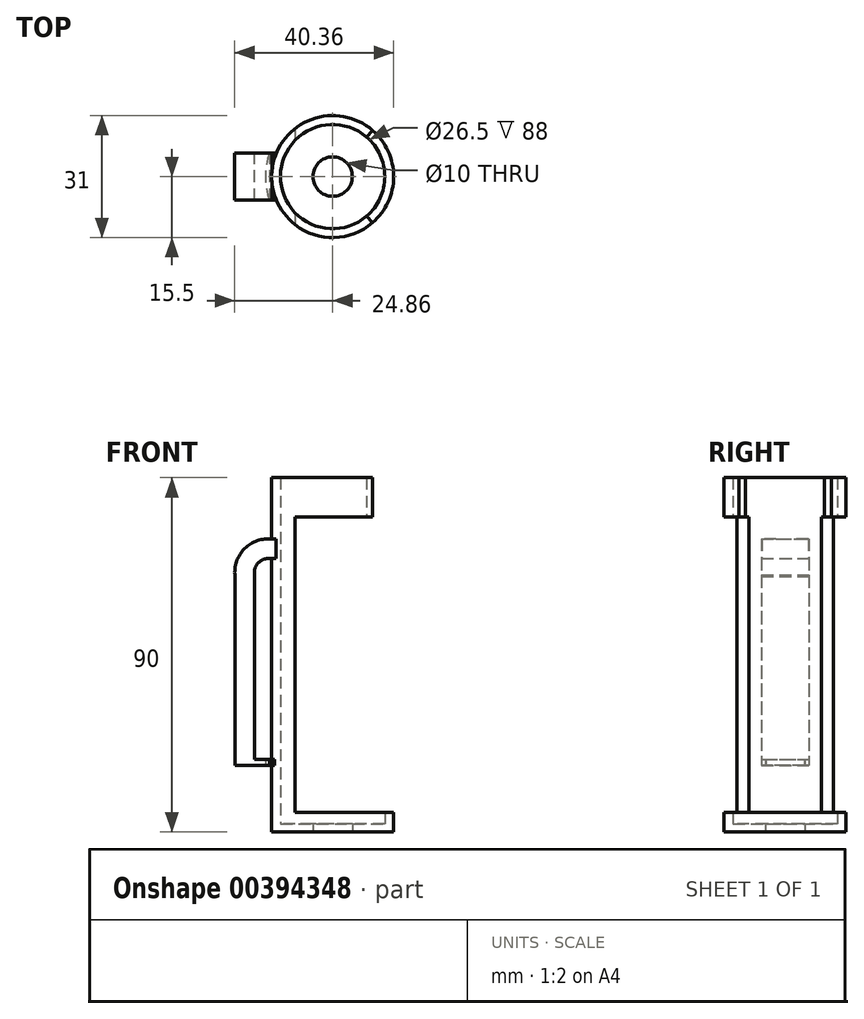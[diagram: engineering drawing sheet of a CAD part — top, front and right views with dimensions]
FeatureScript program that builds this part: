
annotation { "Feature Type Name" : "Feature", "Feature Type Description" : "" }
export const myFeature = defineFeature(function(context is Context, id is Id, definition is map)
    precondition{}
    {
        {
            var Q0;
            Q0=qCreatedBy(makeId("Top.planeOp"),FACE);
            var sketch = newSketch(context, id + "F0", { "sketchPlane" : qUnion([Q0])});
            skCircle(sketch, "E0", {"center": v(0, 0) * mm, "radius": 13.25 * mm});
            skCircle(sketch, "E1", {"center": v(0, 0) * mm, "radius": 15.5 * mm});
            skSolve(sketch);
        }
        {
            var Q0;
            Q0 = qSketchRegion(id + "F0", true);
            extrude(context, id + "F1", {"entities" : qUnion([Q0]), "depth" : 90 * mm});
        }
        {
            var Q0;
            Q0=qCreatedBy(makeId("Top.planeOp"),FACE);
            var sketch = newSketch(context, id + "F2", { "sketchPlane" : qUnion([Q0])});
            skCircle(sketch, "E2", {"center": v(0, 0) * mm, "radius": 15.5 * mm});
            skSolve(sketch);
        }
        {
            var Q0;
            Q0 = qSketchRegion(id + "F2", true);
            extrude(context, id + "F3", {"entities" : qUnion([Q0]), "operationType" : NewBodyOperationType.ADD, "depth" : 2 * mm});
        }
        {
            var Q0;
            Q0=qCreatedBy(makeId("Top.planeOp"),FACE);
            var sketch = newSketch(context, id + "F4", { "sketchPlane" : qUnion([Q0])});
            skCircle(sketch, "E3", {"center": v(0, 0) * mm, "radius": 5 * mm});
            skSolve(sketch);
        }
        {
            var Q0;
            Q0 = qSketchRegion(id + "F4", true);
            extrude(context, id + "F5", {"entities" : qUnion([Q0]), "operationType" : NewBodyOperationType.REMOVE, "endBound" : BoundingType.THROUGH_ALL, "depth" : 25 * mm});
        }
        {
            var Q0;
            Q0=qCreatedBy(makeId("Front.planeOp"),FACE);
            var sketch = newSketch(context, id + "F6", { "sketchPlane" : qUnion([Q0])});
            skLineSegment(sketch, "E4", {"start": v(15.5, 90) * mm, "end": v(15.5, 0) * mm});
            skLineSegment(sketch, "E5", {"start": v(-15.5, 0) * mm, "end": v(-15.5, 90) * mm});
            skLineSegment(sketch, "E6.0", {"start": v(-15.5, 90) * mm, "end": v(15.5, 90) * mm});
            skLineSegment(sketch, "E7.bottom", {"start": v(15.5, 5) * mm, "end": v(-9.5, 5) * mm});
            skLineSegment(sketch, "E7.top", {"start": v(15.5, 80) * mm, "end": v(-9.5, 80) * mm});
            skLineSegment(sketch, "E7.left", {"start": v(15.5, 5) * mm, "end": v(15.5, 80) * mm});
            skLineSegment(sketch, "E7.right", {"start": v(-9.5, 5) * mm, "end": v(-9.5, 80) * mm});
            skSolve(sketch);
        }
        {
            var Q0;
            Q0 = qSketchRegion(id + "F6", true);
            extrude(context, id + "F7", {"entities" : qUnion([Q0]), "operationType" : NewBodyOperationType.REMOVE, "endBound" : BoundingType.SYMMETRIC, "oppositeDirection" : true, "depth" : 60 * mm});
        }
        {
            var Q0;
            Q0=qCreatedBy(makeId("Front.planeOp"),FACE);
            var sketch = newSketch(context, id + "F8", { "sketchPlane" : qUnion([Q0])});
            skArc(sketch, "E8", {"start": v(-15.33, 74.38) * mm, "mid": v(-22.38, 71.97) * mm, "end": v(-24.8, 64.92) * mm});
            skLineSegment(sketch, "E9", {"start": v(-24.8, 64.92) * mm, "end": v(-24.8, 16.9) * mm});
            skLineSegment(sketch, "E10.0", {"start": v(-19.8, 65.3) * mm, "end": v(-19.8, 16.9) * mm});
            skArc(sketch, "E10.1", {"start": v(-15.96, 69.42) * mm, "mid": v(-18.93, 68.35) * mm, "end": v(-19.8, 65.3) * mm});
            skLineSegment(sketch, "E11", {"start": v(-24.8, 16.9) * mm, "end": v(-19.8, 16.9) * mm});
            skLineSegment(sketch, "E12", {"start": v(-15.33, 74.38) * mm, "end": v(-14.33, 74.38) * mm});
            skLineSegment(sketch, "E13", {"start": v(-14.33, 74.38) * mm, "end": v(-14.33, 69.42) * mm});
            skLineSegment(sketch, "E14", {"start": v(-14.33, 69.42) * mm, "end": v(-15.96, 69.42) * mm});
            skSolve(sketch);
        }
        {
            var Q0;
            Q0=makeQuery(id+"F8.imprint","IMPRINT",FACE,{"disambiguationData":[TD([[makeQuery(id+"F8.imprint","IMPRINT",EDGE,{"derivedFrom":sQuery(id+"F8.wireOp",EDGE,"E8")}),1.0]])]});
            var Q1;
            Q1 = qSketchRegion(id + "F10", true);
            extrude(context, id + "F9", {"entities" : qUnion([Q0, Q1]), "operationType" : NewBodyOperationType.ADD, "endBound" : BoundingType.SYMMETRIC, "depth" : 12 * mm, "offsetDistance" : 25 * mm});
        }
        {
            var Q0;
            Q0=qCreatedBy(makeId("Front.planeOp"),FACE);
            var sketch = newSketch(context, id + "F10", { "sketchPlane" : qUnion([Q0])});
            skArc(sketch, "E15.0.0", {"start": v(-15.33, 74.38) * mm, "mid": v(-22.38, 71.97) * mm, "end": v(-24.8, 64.92) * mm});
            skLineSegment(sketch, "E15.0.1", {"start": v(-24.8, 64.92) * mm, "end": v(-24.8, 16.9) * mm});
            skLineSegment(sketch, "E15.0.2", {"start": v(-24.8, 16.9) * mm, "end": v(-19.8, 16.9) * mm});
            skLineSegment(sketch, "E15.0.3", {"start": v(-19.8, 16.9) * mm, "end": v(-19.8, 65.3) * mm});
            skArc(sketch, "E15.0.4", {"start": v(-19.8, 65.3) * mm, "mid": v(-18.93, 68.35) * mm, "end": v(-15.96, 69.42) * mm});
            skLineSegment(sketch, "E15.0.5", {"start": v(-15.96, 69.42) * mm, "end": v(-14.33, 69.42) * mm});
            skLineSegment(sketch, "E15.0.6", {"start": v(-14.33, 69.42) * mm, "end": v(-14.33, 74.38) * mm});
            skLineSegment(sketch, "E15.0.7", {"start": v(-14.33, 74.38) * mm, "end": v(-15.33, 74.38) * mm});
            skLineSegment(sketch, "E16", {"start": v(-19.8, 16.9) * mm, "end": v(-14.71, 16.9) * mm});
            skLineSegment(sketch, "E17", {"start": v(-14.71, 16.9) * mm, "end": v(-14.71, 18.4) * mm});
            skLineSegment(sketch, "E18", {"start": v(-14.71, 18.4) * mm, "end": v(-19.8, 18.4) * mm});
            skSolve(sketch);
        }
        {
            var Q0;
            Q0 = qSketchRegion(id + "F10", true);
            extrude(context, id + "F11", {"entities" : qUnion([Q0]), "operationType" : NewBodyOperationType.ADD, "endBound" : BoundingType.SYMMETRIC, "depth" : 12 * mm, "offsetDistance" : 25 * mm});
        }
        {
            var Q0;
            Q0=qCreatedBy(makeId("Top.planeOp"),FACE);
            var sketch = newSketch(context, id + "F12", { "sketchPlane" : qUnion([Q0])});
            skArc(sketch, "E19", {"start": v(-15.61, 7) * mm, "mid": v(-17.11, 0.16) * mm, "end": v(-15.74, -6.7) * mm});
            skArc(sketch, "E20", {"start": v(-13.87, 7) * mm, "mid": v(-15.54, 0.17) * mm, "end": v(-14.02, -6.7) * mm});
            skLineSegment(sketch, "E21", {"start": v(-14.02, -6.7) * mm, "end": v(-15.74, -6.7) * mm});
            skLineSegment(sketch, "E22", {"start": v(-15.61, 7) * mm, "end": v(-13.87, 7) * mm});
            skPoint(sketch, "E23.orphan", {"position": v(-17.43, -6.7) * mm});
            skPoint(sketch, "E24.orphan", {"position": v(-17.43, 7) * mm});
            skSolve(sketch);
        }
        {
            var Q0;
            Q0=makeQuery(id+"F12.imprint","IMPRINT",FACE,{"disambiguationData":[TD([[makeQuery(id+"F12.imprint","IMPRINT",EDGE,{"derivedFrom":sQuery(id+"F12.wireOp",EDGE,"E19")}),1.0]])]});
            extrude(context, id + "F13", {"entities" : qUnion([Q0]), "operationType" : NewBodyOperationType.REMOVE, "depth" : 25 * mm, "offsetDistance" : 25 * mm});
        }
        {
            var Q0;
            Q0=makeQuery(id+"F1.opExtrude","CAP_FACE",FACE,{"disambiguationData":[OSD([sQuery(id+"F0.wireOp",EDGE,"E0"),sQuery(id+"F0.wireOp",EDGE,"E1")])],"isStart":false});
            var sketch = newSketch(context, id + "F14", { "sketchPlane" : qUnion([Q0])});
            skLineSegment(sketch, "E25", {"start": v(0, 0) * mm, "end": v(11.2, 12.98) * mm});
            skLineSegment(sketch, "E26.MirrorCS", {"start": v(0, 0) * mm, "end": v(11.2, -12.98) * mm});
            skArc(sketch, "E27", {"start": v(11.2, -12.98) * mm, "mid": v(17.14, 0) * mm, "end": v(11.2, 12.98) * mm});
            skPoint(sketch, "E28.orphan", {"position": v(10.12, 11.74) * mm});
            skPoint(sketch, "E29.orphan", {"position": v(10.12, -11.74) * mm});
            skSolve(sketch);
        }
        {
            var Q0;
            Q0 = qSketchRegion(id + "F14", true);
            extrude(context, id + "F15", {"entities" : qUnion([Q0]), "operationType" : NewBodyOperationType.REMOVE, "oppositeDirection" : true, "depth" : 25 * mm, "offsetDistance" : 25 * mm});
        }
        {
            var Q0;
            {var subQ0=sQuery(id+"F14.wireOp",EDGE,"E25");var subQ1=makeQuery(id+"F1.opExtrude","CAP_EDGE",EDGE,{"disambiguationData":[OSD([sQuery(id+"F0.wireOp",EDGE,"E1")])],"isStart":false});var subQ2=makeQuery(id+"F14.imprint","INTERSECT",VERTEX,{"derivedFrom":[subQ1,subQ0]});Q0=makeQuery(id+"F14.imprint","IMPRINT",FACE,{"disambiguationData":[TD([[makeQuery(id+"F14.imprint","IMPRINT",EDGE,{"disambiguationData":[TD([[subQ2,1.0]])],"derivedFrom":subQ0}),-1.0]])]});}
            var Q1;
            {var subQ0=sQuery(id+"F14.wireOp",EDGE,"E27");Q1=makeQuery(id+"F14.imprint","IMPRINT",FACE,{"disambiguationData":[TD([[makeQuery(id+"F14.imprint","IMPRINT",EDGE,{"derivedFrom":subQ0}),1.0]])]});}
            var Q2;
            {var subQ0=sQuery(id+"F14.wireOp",EDGE,"E26.MirrorCS");var subQ1=sQuery(id+"F14.wireOp",EDGE,"E25");var subQ2=makeQuery(id+"F14.imprint","INTERSECT",VERTEX,{"derivedFrom":[subQ1,subQ0]});Q2=makeQuery(id+"F14.imprint","IMPRINT",FACE,{"disambiguationData":[TD([[makeQuery(id+"F14.imprint","IMPRINT",EDGE,{"disambiguationData":[TD([[subQ2,-1.0]])],"derivedFrom":subQ1}),-1.0]])]});}
            extrude(context, id + "F16", {"entities" : qUnion([Q0, Q1, Q2]), "operationType" : NewBodyOperationType.REMOVE, "oppositeDirection" : true, "depth" : 25 * mm, "offsetDistance" : 25 * mm});
        }
    });
